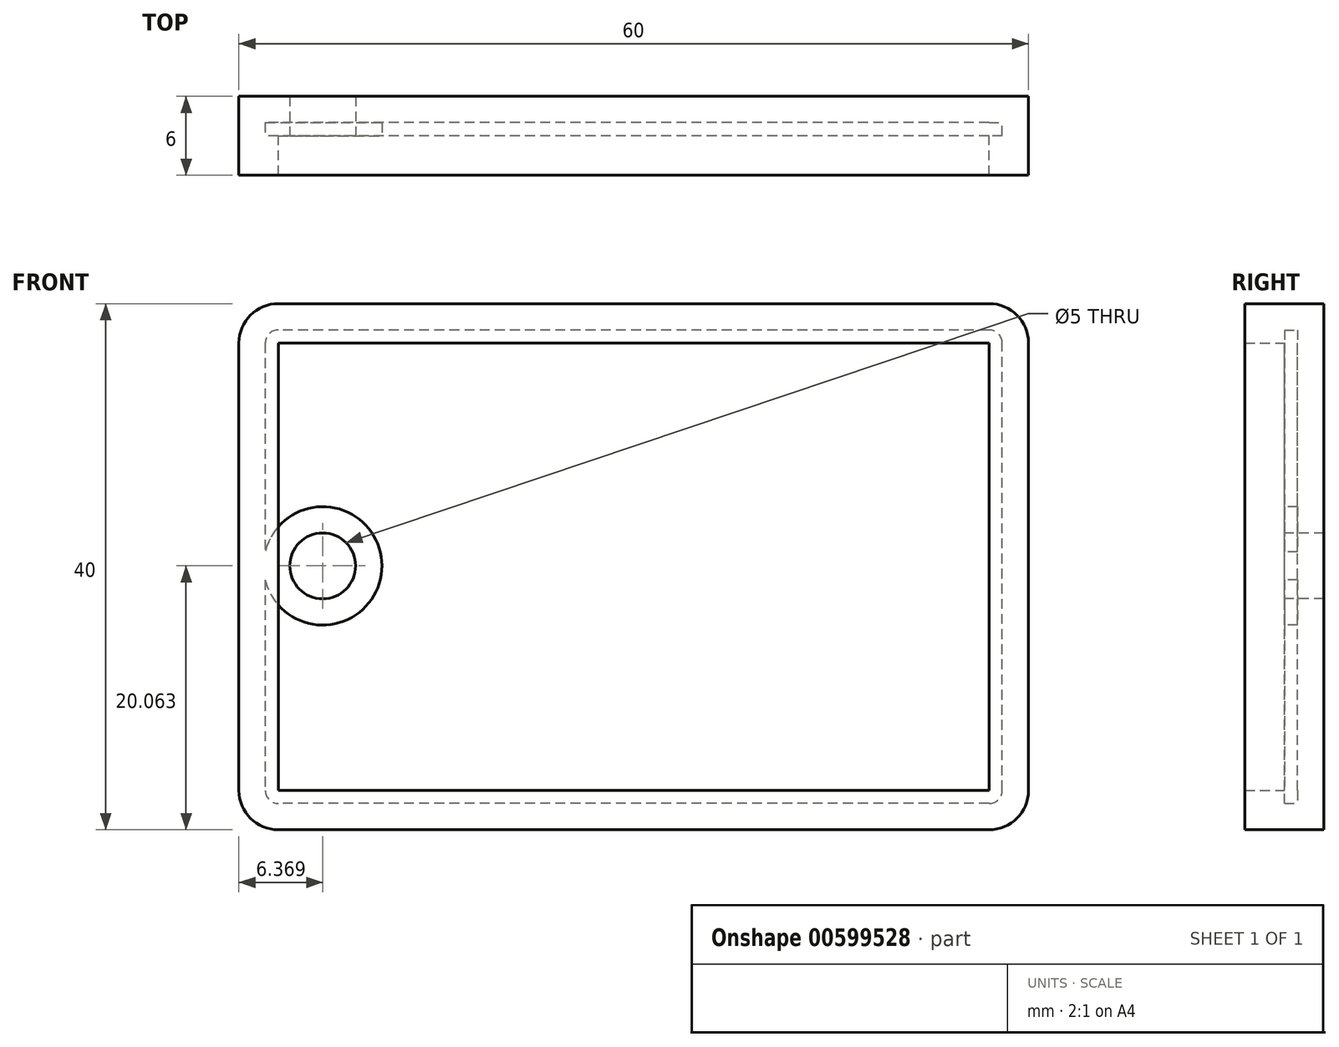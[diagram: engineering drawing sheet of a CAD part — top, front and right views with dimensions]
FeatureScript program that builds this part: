
annotation { "Feature Type Name" : "Feature", "Feature Type Description" : "" }
export const myFeature = defineFeature(function(context is Context, id is Id, definition is map)
    precondition{}
    {
        {
            var Q0;
            Q0=qCreatedBy(makeId("Front.planeOp"),FACE);
            var sketch = newSketch(context, id + "F0", { "sketchPlane" : qUnion([Q0])});
            skLineSegment(sketch, "E0.bottom", {"start": v(30, -20) * mm, "end": v(-30, -20) * mm});
            skLineSegment(sketch, "E0.top", {"start": v(30, 20) * mm, "end": v(-30, 20) * mm});
            skLineSegment(sketch, "E0.left", {"start": v(30, -20) * mm, "end": v(30, 20) * mm});
            skLineSegment(sketch, "E0.right", {"start": v(-30, -20) * mm, "end": v(-30, 20) * mm});
            skPoint(sketch, "E0.middle", {"position": v(0, 0) * mm});
            skSolve(sketch);
        }
        {
            var Q0;
            Q0=makeQuery(id+"F0.imprint","IMPRINT",FACE,{"disambiguationData":[TD([[makeQuery(id+"F0.imprint","IMPRINT",EDGE,{"derivedFrom":sQuery(id+"F0.wireOp",EDGE,"E0.bottom")}),-1.0]])]});
            extrude(context, id + "F1", {"entities" : qUnion([Q0]), "oppositeDirection" : true, "depth" : 6 * mm, "offsetDistance" : 25 * mm, "symmetric" : true});
        }
        {
            var Q0;
            Q0=makeQuery(id+"F1.opExtrude","SWEPT_EDGE",EDGE,{"disambiguationData":[OSD([sQuery(id+"F0.wireOp",EDGE,"E0.bottom"),sQuery(id+"F0.wireOp",EDGE,"E0.right")])]});
            var Q1;
            Q1=makeQuery(id+"F1.opExtrude","SWEPT_EDGE",EDGE,{"disambiguationData":[OSD([sQuery(id+"F0.wireOp",EDGE,"E0.bottom"),sQuery(id+"F0.wireOp",EDGE,"E0.left")])]});
            var Q2;
            Q2=makeQuery(id+"F1.opExtrude","SWEPT_EDGE",EDGE,{"disambiguationData":[OSD([sQuery(id+"F0.wireOp",EDGE,"E0.top"),sQuery(id+"F0.wireOp",EDGE,"E0.right")])]});
            var Q3;
            Q3=makeQuery(id+"F1.opExtrude","SWEPT_EDGE",EDGE,{"disambiguationData":[OSD([sQuery(id+"F0.wireOp",EDGE,"E0.top"),sQuery(id+"F0.wireOp",EDGE,"E0.left")])]});
            fillet(context, id + "F2", {"entities" : qUnion([Q0, Q1, Q2, Q3]), "radius" : 3 * mm, "tangentPropagation" : true, "allowEdgeOverflow" : false});
        }
        {
            var Q0;
            Q0=makeQuery(id+"F1.opExtrude","CAP_FACE",FACE,{"disambiguationData":[OSD([sQuery(id+"F0.wireOp",EDGE,"E0.bottom"),sQuery(id+"F0.wireOp",EDGE,"E0.top"),sQuery(id+"F0.wireOp",EDGE,"E0.left"),sQuery(id+"F0.wireOp",EDGE,"E0.right")])],"isStart":true});
            shell(context, id + "F3", {"entities" : qUnion([Q0]), "thickness" : 3 * mm});
        }
        {
            var Q0;
            Q0=makeQuery(id+"F3.opShell","OFFSET_FACE",FACE,{"disambiguationData":[OSD([sQuery(id+"F0.wireOp",EDGE,"E0.bottom"),sQuery(id+"F0.wireOp",EDGE,"E0.top"),sQuery(id+"F0.wireOp",EDGE,"E0.left"),sQuery(id+"F0.wireOp",EDGE,"E0.right")])]});
            var sketch = newSketch(context, id + "F4", { "sketchPlane" : qUnion([Q0])});
            skCircle(sketch, "E1", {"center": v(-23.63, 0.06) * mm, "radius": 3.37 * mm});
            skPoint(sketch, "E1.first.point", {"position": v(-27, 0) * mm});
            skPoint(sketch, "E1.second.point", {"position": v(-21.43, 2.62) * mm});
            skPoint(sketch, "E1.third.point", {"position": v(-20.85, -1.84) * mm});
            skSolve(sketch);
        }
        {
            var Q0;
            Q0=sQuery(id+"F4.wireOp",VERTEX,"E1.center");
            var Q1;
            Q1=makeQuery(id+"F1.opExtrude","SWEPT_BODY",BODY,{"disambiguationData":[OSD([sQuery(id+"F0.wireOp",EDGE,"E0.bottom"),sQuery(id+"F0.wireOp",EDGE,"E0.top"),sQuery(id+"F0.wireOp",EDGE,"E0.left"),sQuery(id+"F0.wireOp",EDGE,"E0.right")])]});
            hole(context, id + "F5", {"style" : HoleStyle.SIMPLE, "endStyle" : HoleEndStyle.THROUGH, "holeDiameter" : 5 * mm, "majorDiameter" : 5 * mm, "isTappedThrough" : true, "tappedDepth" : 12 * mm, "tapClearance" : 3, "locations" : qUnion([Q0]), "scope" : qUnion([Q1])});
        }
        {
            var Q0;
            Q0=makeQuery(id+"F3.opShell","OFFSET_FACE",FACE,{"disambiguationData":[OSD([sQuery(id+"F0.wireOp",EDGE,"E0.bottom"),sQuery(id+"F0.wireOp",EDGE,"E0.top"),sQuery(id+"F0.wireOp",EDGE,"E0.left"),sQuery(id+"F0.wireOp",EDGE,"E0.right")])]});
            shell(context, id + "F6", {"entities" : qUnion([Q0]), "thickness" : 2 * mm});
        }
    });
